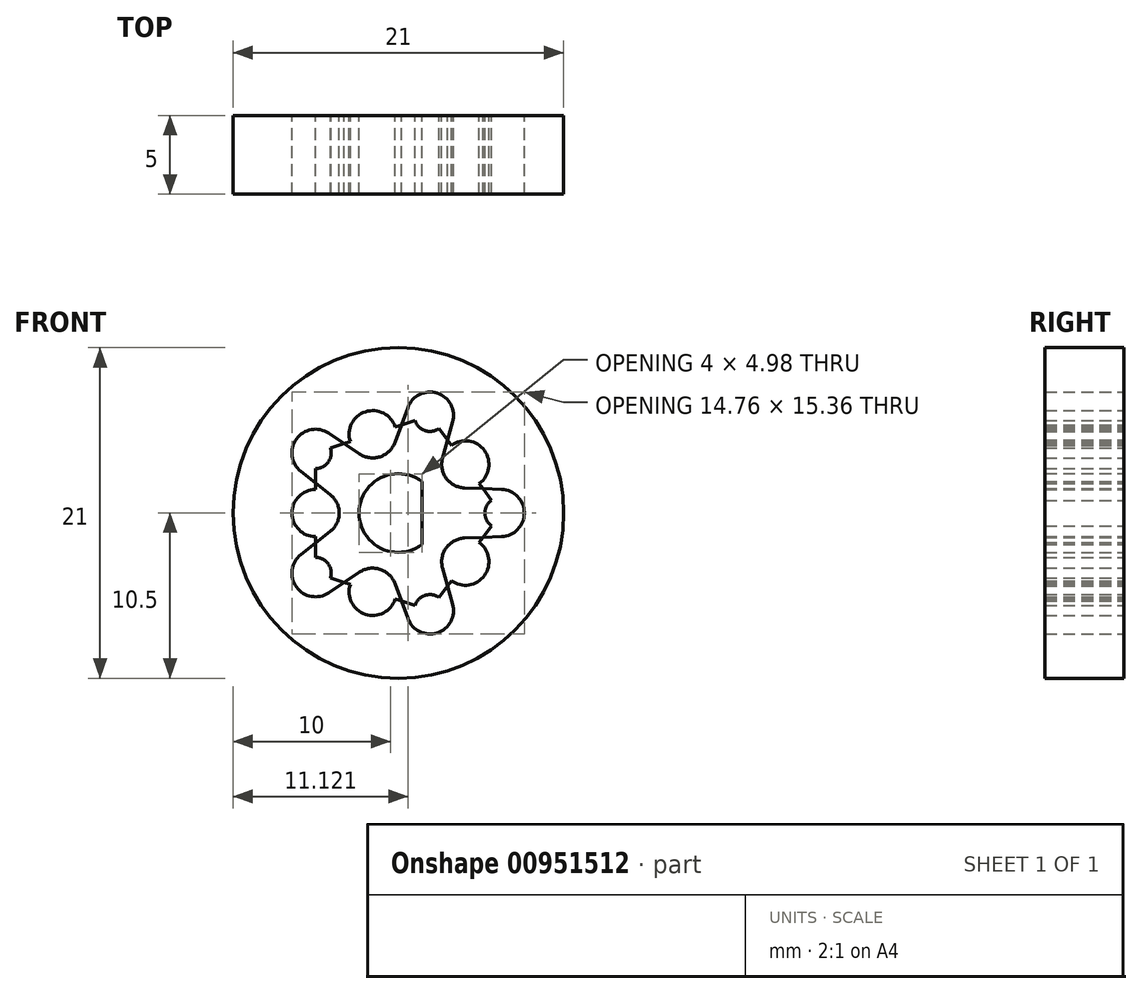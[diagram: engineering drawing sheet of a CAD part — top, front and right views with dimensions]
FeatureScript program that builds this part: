
annotation { "Feature Type Name" : "Feature", "Feature Type Description" : "" }
export const myFeature = defineFeature(function(context is Context, id is Id, definition is map)
    precondition{}
    {
        {
            var Q0;
            Q0=qCreatedBy(makeId("Front.planeOp"),FACE);
            var sketch = newSketch(context, id + "F0", { "sketchPlane" : qUnion([Q0])});
            skCircle(sketch, "E0", {"center": v(0, 0) * mm, "radius": 2.5 * mm});
            skCircle(sketch, "E1.cCircle", {"center": v(0, 0) * mm, "radius": 5.26 * mm, "construction": true});
            skLineSegment(sketch, "E1.0", {"start": v(-5.26, -3.82) * mm, "end": v(-5.26, 3.82) * mm});
            skLineSegment(sketch, "E1.1", {"start": v(-5.26, 3.82) * mm, "end": v(2, 6.18) * mm});
            skLineSegment(sketch, "E1.2", {"start": v(2, 6.18) * mm, "end": v(6.5, 0) * mm});
            skLineSegment(sketch, "E1.3", {"start": v(6.5, 0) * mm, "end": v(2, -6.18) * mm});
            skLineSegment(sketch, "E1.4", {"start": v(2, -6.18) * mm, "end": v(-5.26, -3.82) * mm});
            skPoint(sketch, "E1.0.midPoint", {"position": v(-5.26, 0) * mm});
            skCircle(sketch, "E2", {"center": v(-5.26, 3.82) * mm, "radius": 1 * mm});
            skCircle(sketch, "E3", {"center": v(2, 6.18) * mm, "radius": 1 * mm});
            skCircle(sketch, "E4", {"center": v(6.5, 0) * mm, "radius": 1 * mm});
            skCircle(sketch, "E5", {"center": v(2, -6.18) * mm, "radius": 1 * mm});
            skCircle(sketch, "E6", {"center": v(-5.26, -3.82) * mm, "radius": 1 * mm});
            skCircle(sketch, "E7", {"center": v(-5.26, 3.82) * mm, "radius": 1.5 * mm});
            skCircle(sketch, "E8", {"center": v(2, 6.18) * mm, "radius": 1.5 * mm});
            skCircle(sketch, "E9", {"center": v(6.5, 0) * mm, "radius": 1.5 * mm});
            skCircle(sketch, "E10", {"center": v(2, -6.18) * mm, "radius": 1.5 * mm});
            skCircle(sketch, "E11", {"center": v(-5.26, -3.82) * mm, "radius": 1.5 * mm});
            skCircle(sketch, "E12", {"center": v(-5.26, 0) * mm, "radius": 1.5 * mm});
            skCircle(sketch, "E13", {"center": v(-1.62, 5) * mm, "radius": 1.5 * mm});
            skCircle(sketch, "E14", {"center": v(4.25, 3.1) * mm, "radius": 1.5 * mm});
            skCircle(sketch, "E15", {"center": v(4.25, -3.1) * mm, "radius": 1.5 * mm});
            skCircle(sketch, "E16", {"center": v(-1.62, -5) * mm, "radius": 1.5 * mm});
            skLineSegment(sketch, "E17", {"start": v(-6.19, 2.64) * mm, "end": v(-4.33, 1.18) * mm});
            skLineSegment(sketch, "E18", {"start": v(-4.33, -1.18) * mm, "end": v(-6.19, -2.64) * mm});
            skLineSegment(sketch, "E19", {"start": v(-4.43, -5.07) * mm, "end": v(-2.46, -3.75) * mm});
            skLineSegment(sketch, "E20", {"start": v(-0.22, -4.48) * mm, "end": v(0.6, -6.7) * mm});
            skLineSegment(sketch, "E21", {"start": v(3.45, -5.77) * mm, "end": v(2.81, -3.5) * mm});
            skLineSegment(sketch, "E22", {"start": v(4.2, -1.6) * mm, "end": v(6.56, -1.5) * mm});
            skLineSegment(sketch, "E23", {"start": v(6.56, 1.5) * mm, "end": v(4.2, 1.6) * mm});
            skLineSegment(sketch, "E24", {"start": v(2.81, 3.5) * mm, "end": v(3.45, 5.77) * mm});
            skLineSegment(sketch, "E25", {"start": v(0.6, 6.7) * mm, "end": v(-0.22, 4.48) * mm});
            skLineSegment(sketch, "E26", {"start": v(-2.46, 3.75) * mm, "end": v(-4.43, 5.07) * mm});
            skLineSegment(sketch, "E27", {"start": v(1.5, 2) * mm, "end": v(1.5, -2) * mm});
            skCircle(sketch, "E28", {"center": v(0, 0) * mm, "radius": 10.5 * mm});
            skSolve(sketch);
        }
        {
            var Q0;
            {var subQ25=sQuery(id+"F0.wireOp",EDGE,"I007ogCC-rbbc-wW61-PL4D-8xOWQatjkpYn");var subQ26=sQuery(id+"F0.wireOp",EDGE,"E0");var subQ27=makeQuery(id+"F0.imprint","INTERSECT",VERTEX,{"disambiguationData":[OD(0.0)],"derivedFrom":[subQ26,subQ25]});Q0=makeQuery(id+"F0.imprint","IMPRINT",FACE,{"disambiguationData":[TD([[makeQuery(id+"F0.imprint","IMPRINT",EDGE,{"disambiguationData":[TD([[subQ27,1.0]])],"derivedFrom":subQ26}),-1.0]])]});}
            var Q1;
            {var subQ0=sQuery(id+"F0.wireOp",EDGE,"I007ogCC-rbbc-wW61-PL4D-8xOWQatjkpYn");Q1=makeQuery(id+"F0.imprint","IMPRINT",FACE,{"disambiguationData":[TD([[makeQuery(id+"F0.imprint","IMPRINT",EDGE,{"derivedFrom":subQ0}),1.0]])]});}
            var Q2;
            {var subQ0=sQuery(id+"F0.wireOp",EDGE,"E1.0");var subQ1=sQuery(id+"F0.wireOp",EDGE,"E2");var subQ2=makeQuery(id+"F0.imprint","INTERSECT",VERTEX,{"derivedFrom":[subQ1,subQ0]});Q2=makeQuery(id+"F0.imprint","IMPRINT",FACE,{"disambiguationData":[TD([[makeQuery(id+"F0.imprint","IMPRINT",EDGE,{"disambiguationData":[TD([[subQ2,-1.0]])],"derivedFrom":subQ1}),-1.0]])]});}
            var Q3;
            {var subQ0=sQuery(id+"F0.wireOp",EDGE,"E1.0");var subQ1=sQuery(id+"F0.wireOp",EDGE,"E2");var subQ2=makeQuery(id+"F0.imprint","INTERSECT",VERTEX,{"derivedFrom":[subQ1,subQ0]});Q3=makeQuery(id+"F0.imprint","IMPRINT",FACE,{"disambiguationData":[TD([[makeQuery(id+"F0.imprint","IMPRINT",EDGE,{"disambiguationData":[TD([[subQ2,1.0]])],"derivedFrom":subQ1}),-1.0]])]});}
            var Q4;
            {var subQ0=sQuery(id+"F0.wireOp",EDGE,"E1.1");var subQ1=sQuery(id+"F0.wireOp",EDGE,"E3");var subQ2=makeQuery(id+"F0.imprint","INTERSECT",VERTEX,{"derivedFrom":[subQ1,subQ0]});Q4=makeQuery(id+"F0.imprint","IMPRINT",FACE,{"disambiguationData":[TD([[makeQuery(id+"F0.imprint","IMPRINT",EDGE,{"disambiguationData":[TD([[subQ2,-1.0]])],"derivedFrom":subQ1}),-1.0]])]});}
            var Q5;
            {var subQ2=sQuery(id+"F0.wireOp",EDGE,"E1.1");var subQ4=sQuery(id+"F0.wireOp",EDGE,"E3");var subQ5=makeQuery(id+"F0.imprint","INTERSECT",VERTEX,{"derivedFrom":[subQ4,subQ2]});Q5=makeQuery(id+"F0.imprint","IMPRINT",FACE,{"disambiguationData":[TD([[makeQuery(id+"F0.imprint","IMPRINT",EDGE,{"disambiguationData":[TD([[subQ5,1.0]])],"derivedFrom":subQ4}),-1.0]])]});}
            var Q6;
            {var subQ0=sQuery(id+"F0.wireOp",EDGE,"E1.2");var subQ1=sQuery(id+"F0.wireOp",EDGE,"E4");var subQ2=makeQuery(id+"F0.imprint","INTERSECT",VERTEX,{"derivedFrom":[subQ1,subQ0]});Q6=makeQuery(id+"F0.imprint","IMPRINT",FACE,{"disambiguationData":[TD([[makeQuery(id+"F0.imprint","IMPRINT",EDGE,{"disambiguationData":[TD([[subQ2,-1.0]])],"derivedFrom":subQ1}),-1.0]])]});}
            var Q7;
            {var subQ2=sQuery(id+"F0.wireOp",EDGE,"E1.2");var subQ5=sQuery(id+"F0.wireOp",EDGE,"E4");var subQ8=makeQuery(id+"F0.imprint","INTERSECT",VERTEX,{"derivedFrom":[subQ5,subQ2]});Q7=makeQuery(id+"F0.imprint","IMPRINT",FACE,{"disambiguationData":[TD([[makeQuery(id+"F0.imprint","IMPRINT",EDGE,{"disambiguationData":[TD([[subQ8,1.0]])],"derivedFrom":subQ5}),-1.0]])]});}
            var Q8;
            {var subQ0=sQuery(id+"F0.wireOp",EDGE,"E1.3");var subQ1=sQuery(id+"F0.wireOp",EDGE,"E5");var subQ2=makeQuery(id+"F0.imprint","INTERSECT",VERTEX,{"derivedFrom":[subQ1,subQ0]});Q8=makeQuery(id+"F0.imprint","IMPRINT",FACE,{"disambiguationData":[TD([[makeQuery(id+"F0.imprint","IMPRINT",EDGE,{"disambiguationData":[TD([[subQ2,-1.0]])],"derivedFrom":subQ1}),-1.0]])]});}
            var Q9;
            {var subQ0=sQuery(id+"F0.wireOp",EDGE,"E1.3");var subQ1=sQuery(id+"F0.wireOp",EDGE,"E5");var subQ2=makeQuery(id+"F0.imprint","INTERSECT",VERTEX,{"derivedFrom":[subQ1,subQ0]});Q9=makeQuery(id+"F0.imprint","IMPRINT",FACE,{"disambiguationData":[TD([[makeQuery(id+"F0.imprint","IMPRINT",EDGE,{"disambiguationData":[TD([[subQ2,1.0]])],"derivedFrom":subQ1}),-1.0]])]});}
            var Q10;
            {var subQ0=sQuery(id+"F0.wireOp",EDGE,"E1.0");var subQ1=sQuery(id+"F0.wireOp",EDGE,"E6");var subQ2=makeQuery(id+"F0.imprint","INTERSECT",VERTEX,{"derivedFrom":[subQ1,subQ0]});Q10=makeQuery(id+"F0.imprint","IMPRINT",FACE,{"disambiguationData":[TD([[makeQuery(id+"F0.imprint","IMPRINT",EDGE,{"disambiguationData":[TD([[subQ2,1.0]])],"derivedFrom":subQ1}),-1.0]])]});}
            var Q11;
            {var subQ2=sQuery(id+"F0.wireOp",EDGE,"E1.0");var subQ4=sQuery(id+"F0.wireOp",EDGE,"E6");var subQ5=makeQuery(id+"F0.imprint","INTERSECT",VERTEX,{"derivedFrom":[subQ4,subQ2]});Q11=makeQuery(id+"F0.imprint","IMPRINT",FACE,{"disambiguationData":[TD([[makeQuery(id+"F0.imprint","IMPRINT",EDGE,{"disambiguationData":[TD([[subQ5,-1.0]])],"derivedFrom":subQ4}),-1.0]])]});}
            var Q12;
            {var subQ0=sQuery(id+"F0.wireOp",EDGE,"E18");var subQ1=sQuery(id+"F0.wireOp",EDGE,"E1.0");var subQ2=makeQuery(id+"F0.imprint","INTERSECT",VERTEX,{"derivedFrom":[subQ1,subQ0]});Q12=makeQuery(id+"F0.imprint","IMPRINT",FACE,{"disambiguationData":[TD([[makeQuery(id+"F0.imprint","IMPRINT",EDGE,{"disambiguationData":[TD([[subQ2,1.0]])],"derivedFrom":subQ1}),1.0]])]});}
            var Q13;
            {var subQ0=sQuery(id+"F0.wireOp",EDGE,"E17");var subQ1=sQuery(id+"F0.wireOp",EDGE,"E1.0");var subQ2=makeQuery(id+"F0.imprint","INTERSECT",VERTEX,{"derivedFrom":[subQ1,subQ0]});Q13=makeQuery(id+"F0.imprint","IMPRINT",FACE,{"disambiguationData":[TD([[makeQuery(id+"F0.imprint","IMPRINT",EDGE,{"disambiguationData":[TD([[subQ2,-1.0]])],"derivedFrom":subQ1}),1.0]])]});}
            var Q14;
            {var subQ0=sQuery(id+"F0.wireOp",EDGE,"E26");var subQ1=sQuery(id+"F0.wireOp",EDGE,"E1.1");var subQ2=makeQuery(id+"F0.imprint","INTERSECT",VERTEX,{"derivedFrom":[subQ1,subQ0]});Q14=makeQuery(id+"F0.imprint","IMPRINT",FACE,{"disambiguationData":[TD([[makeQuery(id+"F0.imprint","IMPRINT",EDGE,{"disambiguationData":[TD([[subQ2,1.0]])],"derivedFrom":subQ1}),1.0]])]});}
            var Q15;
            {var subQ0=sQuery(id+"F0.wireOp",EDGE,"E25");var subQ1=sQuery(id+"F0.wireOp",EDGE,"E1.1");var subQ2=makeQuery(id+"F0.imprint","INTERSECT",VERTEX,{"derivedFrom":[subQ1,subQ0]});Q15=makeQuery(id+"F0.imprint","IMPRINT",FACE,{"disambiguationData":[TD([[makeQuery(id+"F0.imprint","IMPRINT",EDGE,{"disambiguationData":[TD([[subQ2,-1.0]])],"derivedFrom":subQ1}),1.0]])]});}
            var Q16;
            {var subQ0=sQuery(id+"F0.wireOp",EDGE,"E23");var subQ1=sQuery(id+"F0.wireOp",EDGE,"E1.2");var subQ2=makeQuery(id+"F0.imprint","INTERSECT",VERTEX,{"derivedFrom":[subQ1,subQ0]});Q16=makeQuery(id+"F0.imprint","IMPRINT",FACE,{"disambiguationData":[TD([[makeQuery(id+"F0.imprint","IMPRINT",EDGE,{"disambiguationData":[TD([[subQ2,-1.0]])],"derivedFrom":subQ1}),1.0]])]});}
            var Q17;
            {var subQ0=sQuery(id+"F0.wireOp",EDGE,"E22");var subQ1=sQuery(id+"F0.wireOp",EDGE,"E1.3");var subQ2=makeQuery(id+"F0.imprint","INTERSECT",VERTEX,{"derivedFrom":[subQ1,subQ0]});Q17=makeQuery(id+"F0.imprint","IMPRINT",FACE,{"disambiguationData":[TD([[makeQuery(id+"F0.imprint","IMPRINT",EDGE,{"disambiguationData":[TD([[subQ2,1.0]])],"derivedFrom":subQ1}),1.0]])]});}
            var Q18;
            {var subQ0=sQuery(id+"F0.wireOp",EDGE,"E21");var subQ1=sQuery(id+"F0.wireOp",EDGE,"E1.3");var subQ2=makeQuery(id+"F0.imprint","INTERSECT",VERTEX,{"derivedFrom":[subQ1,subQ0]});Q18=makeQuery(id+"F0.imprint","IMPRINT",FACE,{"disambiguationData":[TD([[makeQuery(id+"F0.imprint","IMPRINT",EDGE,{"disambiguationData":[TD([[subQ2,-1.0]])],"derivedFrom":subQ1}),1.0]])]});}
            var Q19;
            {var subQ0=sQuery(id+"F0.wireOp",EDGE,"E20");var subQ1=sQuery(id+"F0.wireOp",EDGE,"E1.4");var subQ2=makeQuery(id+"F0.imprint","INTERSECT",VERTEX,{"derivedFrom":[subQ1,subQ0]});Q19=makeQuery(id+"F0.imprint","IMPRINT",FACE,{"disambiguationData":[TD([[makeQuery(id+"F0.imprint","IMPRINT",EDGE,{"disambiguationData":[TD([[subQ2,1.0]])],"derivedFrom":subQ1}),1.0]])]});}
            var Q20;
            {var subQ0=sQuery(id+"F0.wireOp",EDGE,"E19");var subQ1=sQuery(id+"F0.wireOp",EDGE,"E1.4");var subQ2=makeQuery(id+"F0.imprint","INTERSECT",VERTEX,{"derivedFrom":[subQ1,subQ0]});Q20=makeQuery(id+"F0.imprint","IMPRINT",FACE,{"disambiguationData":[TD([[makeQuery(id+"F0.imprint","IMPRINT",EDGE,{"disambiguationData":[TD([[subQ2,-1.0]])],"derivedFrom":subQ1}),1.0]])]});}
            var Q21;
            {var subQ0=sQuery(id+"F0.wireOp",EDGE,"E24");var subQ1=sQuery(id+"F0.wireOp",EDGE,"E1.2");var subQ2=makeQuery(id+"F0.imprint","INTERSECT",VERTEX,{"derivedFrom":[subQ1,subQ0]});Q21=makeQuery(id+"F0.imprint","IMPRINT",FACE,{"disambiguationData":[TD([[makeQuery(id+"F0.imprint","IMPRINT",EDGE,{"disambiguationData":[TD([[subQ2,1.0]])],"derivedFrom":subQ1}),1.0]])]});}
            var Q22;
            {var subQ0=sQuery(id+"F0.wireOp",EDGE,"E27");Q22=makeQuery(id+"F0.imprint","IMPRINT",FACE,{"disambiguationData":[TD([[makeQuery(id+"F0.imprint","IMPRINT",EDGE,{"derivedFrom":subQ0}),1.0]])]});}
            var Q23;
            Q23=makeQuery(id+"F0.imprint","IMPRINT",FACE,{"disambiguationData":[TD([[makeQuery(id+"F0.imprint","IMPRINT",EDGE,{"derivedFrom":sQuery(id+"F0.wireOp",EDGE,"E28")}),1.0]])]});
            var Q24;
            {var subQ0=sQuery(id+"F0.wireOp",EDGE,"E16");var subQ1=sQuery(id+"F0.wireOp",EDGE,"E1.4");var subQ2=makeQuery(id+"F0.imprint","INTERSECT",VERTEX,{"disambiguationData":[OD(1.0)],"derivedFrom":[subQ1,subQ0]});Q24=makeQuery(id+"F0.imprint","IMPRINT",FACE,{"disambiguationData":[TD([[makeQuery(id+"F0.imprint","IMPRINT",EDGE,{"disambiguationData":[TD([[subQ2,-1.0]])],"derivedFrom":subQ1}),-1.0]])]});}
            var Q25;
            {var subQ0=sQuery(id+"F0.wireOp",EDGE,"E20");var subQ1=sQuery(id+"F0.wireOp",EDGE,"E1.4");var subQ2=makeQuery(id+"F0.imprint","INTERSECT",VERTEX,{"derivedFrom":[subQ1,subQ0]});Q25=makeQuery(id+"F0.imprint","IMPRINT",FACE,{"disambiguationData":[TD([[makeQuery(id+"F0.imprint","IMPRINT",EDGE,{"disambiguationData":[TD([[subQ2,-1.0]])],"derivedFrom":subQ1}),-1.0]])]});}
            var Q26;
            {var subQ0=sQuery(id+"F0.wireOp",EDGE,"E18");var subQ1=sQuery(id+"F0.wireOp",EDGE,"E1.0");var subQ2=makeQuery(id+"F0.imprint","INTERSECT",VERTEX,{"derivedFrom":[subQ1,subQ0]});Q26=makeQuery(id+"F0.imprint","IMPRINT",FACE,{"disambiguationData":[TD([[makeQuery(id+"F0.imprint","IMPRINT",EDGE,{"disambiguationData":[TD([[subQ2,-1.0]])],"derivedFrom":subQ1}),-1.0]])]});}
            var Q27;
            {var subQ0=sQuery(id+"F0.wireOp",EDGE,"E12");var subQ1=sQuery(id+"F0.wireOp",EDGE,"E1.0");var subQ2=makeQuery(id+"F0.imprint","INTERSECT",VERTEX,{"disambiguationData":[OD(1.0)],"derivedFrom":[subQ1,subQ0]});Q27=makeQuery(id+"F0.imprint","IMPRINT",FACE,{"disambiguationData":[TD([[makeQuery(id+"F0.imprint","IMPRINT",EDGE,{"disambiguationData":[TD([[subQ2,-1.0]])],"derivedFrom":subQ1}),-1.0]])]});}
            var Q28;
            {var subQ0=sQuery(id+"F0.wireOp",EDGE,"E26");var subQ1=sQuery(id+"F0.wireOp",EDGE,"E1.1");var subQ2=makeQuery(id+"F0.imprint","INTERSECT",VERTEX,{"derivedFrom":[subQ1,subQ0]});Q28=makeQuery(id+"F0.imprint","IMPRINT",FACE,{"disambiguationData":[TD([[makeQuery(id+"F0.imprint","IMPRINT",EDGE,{"disambiguationData":[TD([[subQ2,-1.0]])],"derivedFrom":subQ1}),-1.0]])]});}
            var Q29;
            {var subQ0=sQuery(id+"F0.wireOp",EDGE,"E13");var subQ1=sQuery(id+"F0.wireOp",EDGE,"E1.1");var subQ2=makeQuery(id+"F0.imprint","INTERSECT",VERTEX,{"disambiguationData":[OD(1.0)],"derivedFrom":[subQ1,subQ0]});Q29=makeQuery(id+"F0.imprint","IMPRINT",FACE,{"disambiguationData":[TD([[makeQuery(id+"F0.imprint","IMPRINT",EDGE,{"disambiguationData":[TD([[subQ2,-1.0]])],"derivedFrom":subQ1}),-1.0]])]});}
            var Q30;
            {var subQ0=sQuery(id+"F0.wireOp",EDGE,"E24");var subQ1=sQuery(id+"F0.wireOp",EDGE,"E1.2");var subQ2=makeQuery(id+"F0.imprint","INTERSECT",VERTEX,{"derivedFrom":[subQ1,subQ0]});Q30=makeQuery(id+"F0.imprint","IMPRINT",FACE,{"disambiguationData":[TD([[makeQuery(id+"F0.imprint","IMPRINT",EDGE,{"disambiguationData":[TD([[subQ2,-1.0]])],"derivedFrom":subQ1}),-1.0]])]});}
            var Q31;
            {var subQ0=sQuery(id+"F0.wireOp",EDGE,"E14");var subQ1=sQuery(id+"F0.wireOp",EDGE,"E1.2");var subQ2=makeQuery(id+"F0.imprint","INTERSECT",VERTEX,{"disambiguationData":[OD(1.0)],"derivedFrom":[subQ1,subQ0]});Q31=makeQuery(id+"F0.imprint","IMPRINT",FACE,{"disambiguationData":[TD([[makeQuery(id+"F0.imprint","IMPRINT",EDGE,{"disambiguationData":[TD([[subQ2,-1.0]])],"derivedFrom":subQ1}),-1.0]])]});}
            var Q32;
            {var subQ0=sQuery(id+"F0.wireOp",EDGE,"E22");var subQ1=sQuery(id+"F0.wireOp",EDGE,"E1.3");var subQ2=makeQuery(id+"F0.imprint","INTERSECT",VERTEX,{"derivedFrom":[subQ1,subQ0]});Q32=makeQuery(id+"F0.imprint","IMPRINT",FACE,{"disambiguationData":[TD([[makeQuery(id+"F0.imprint","IMPRINT",EDGE,{"disambiguationData":[TD([[subQ2,-1.0]])],"derivedFrom":subQ1}),-1.0]])]});}
            var Q33;
            {var subQ0=sQuery(id+"F0.wireOp",EDGE,"E15");var subQ1=sQuery(id+"F0.wireOp",EDGE,"E1.3");var subQ2=makeQuery(id+"F0.imprint","INTERSECT",VERTEX,{"disambiguationData":[OD(1.0)],"derivedFrom":[subQ1,subQ0]});Q33=makeQuery(id+"F0.imprint","IMPRINT",FACE,{"disambiguationData":[TD([[makeQuery(id+"F0.imprint","IMPRINT",EDGE,{"disambiguationData":[TD([[subQ2,-1.0]])],"derivedFrom":subQ1}),-1.0]])]});}
            extrude(context, id + "F1", {"entities" : qUnion([Q0, Q1, Q2, Q3, Q4, Q5, Q6, Q7, Q8, Q9, Q10, Q11, Q12, Q13, Q14, Q15, Q16, Q17, Q18, Q19, Q20, Q21, Q22, Q23, Q24, Q25, Q26, Q27, Q28, Q29, Q30, Q31, Q32, Q33]), "depth" : 5 * mm, "offsetDistance" : 25 * mm});
        }
    });
